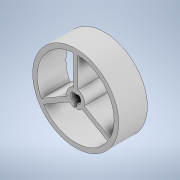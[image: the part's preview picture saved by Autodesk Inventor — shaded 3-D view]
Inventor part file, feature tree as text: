
AUTODESK INVENTOR PART (.ipt)
format: ipt  version: 2022 (Build 260153000, 153)  size: 171,520 bytes
history: native  units: mm
features: sketch x2, other x1, extrude x1, pattern_circular x1, chamfer x1
ambient origin geometry x8: Origin, YZ Plane, XZ Plane, XY Plane, X Axis, Y Axis, Z Axis, Center Point
bodies: Body1 (feature_tree)
feature tree (6):
  other  "ソリッド1"
  extrude  "スポーク"  Depth=1.05mm
  pattern_circular  "円形状パターン1"  [2 undecoded]
  chamfer  "面取り1"  Distance=10.0mm
  sketch  "スケッチ1"
  sketch  "スケッチ2"
note: 2 required parameter values undecoded (feature->parameter linkage not recoverable at this tier; creation-order binding heuristic only, values carry confidence <= 0.55)
